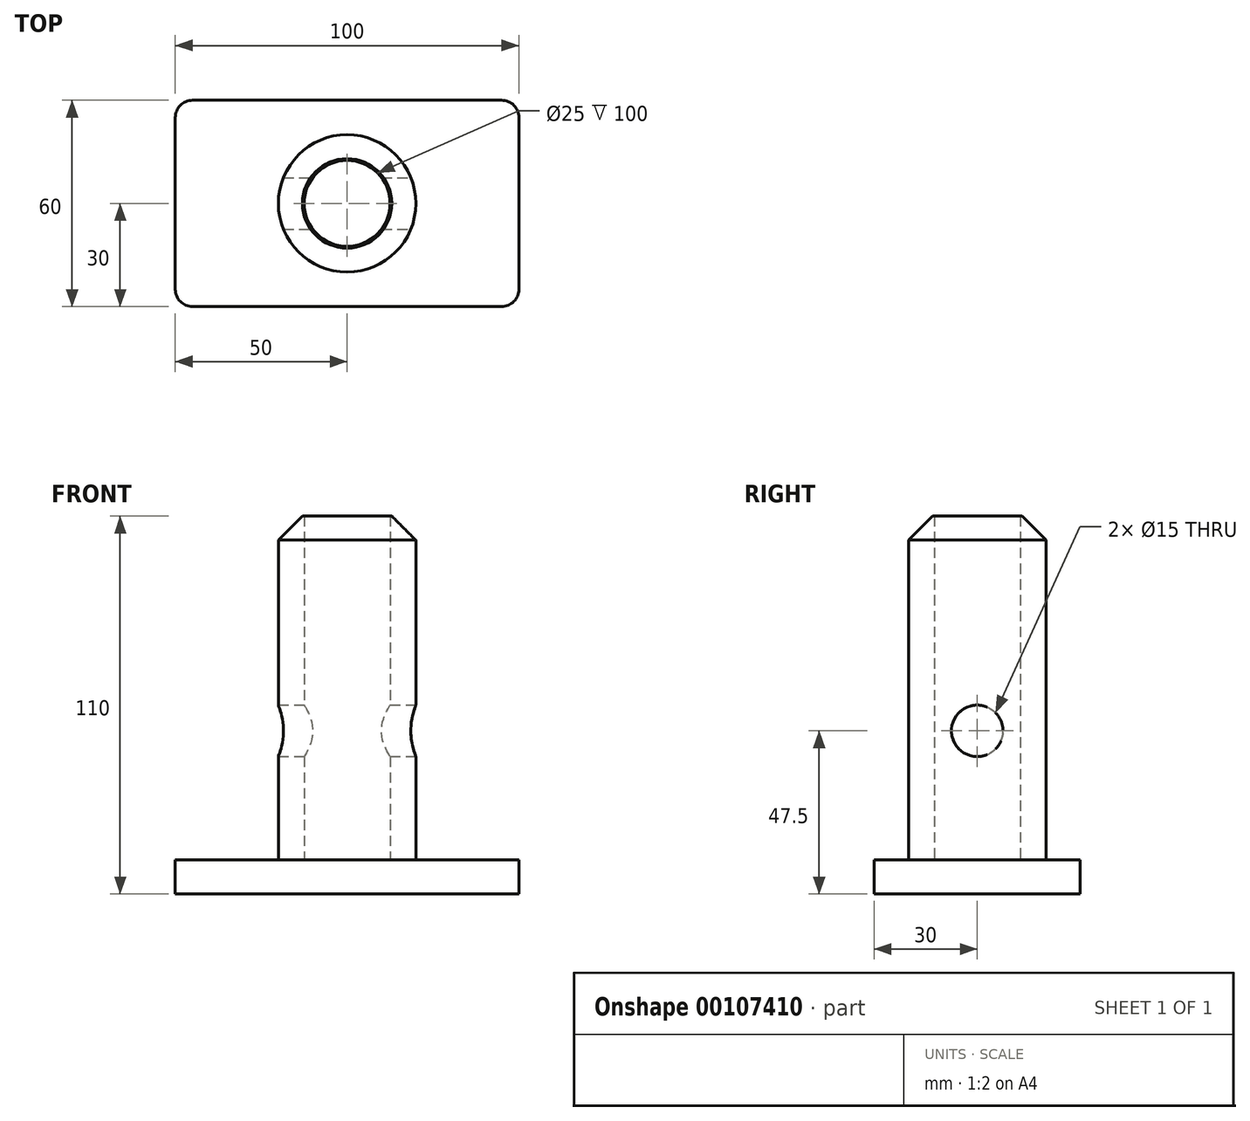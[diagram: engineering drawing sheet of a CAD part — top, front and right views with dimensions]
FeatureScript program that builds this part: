
annotation { "Feature Type Name" : "Feature", "Feature Type Description" : "" }
export const myFeature = defineFeature(function(context is Context, id is Id, definition is map)
    precondition{}
    {
        {
            var Q0;
            Q0=qCreatedBy(makeId("Top.planeOp"),FACE);
            var sketch = newSketch(context, id + "F0", { "sketchPlane" : qUnion([Q0])});
            skCircle(sketch, "E0", {"center": v(0, 0) * mm, "radius": 20 * mm});
            skCircle(sketch, "E1", {"center": v(0, 0) * mm, "radius": 12.5 * mm});
            skSolve(sketch);
        }
        {
            var Q0;
            Q0 = qSketchRegion(id + "F0", true);
            extrude(context, id + "F1", {"entities" : qUnion([Q0]), "depth" : 100 * mm});
        }
        {
            var Q0;
            Q0=qCreatedBy(makeId("Top.planeOp"),FACE);
            var sketch = newSketch(context, id + "F2", { "sketchPlane" : qUnion([Q0])});
            skLineSegment(sketch, "E2.bottom", {"start": v(50, -30) * mm, "end": v(-50, -30) * mm});
            skLineSegment(sketch, "E2.top", {"start": v(50, 30) * mm, "end": v(-50, 30) * mm});
            skLineSegment(sketch, "E2.left", {"start": v(50, -30) * mm, "end": v(50, 30) * mm});
            skLineSegment(sketch, "E2.right", {"start": v(-50, -30) * mm, "end": v(-50, 30) * mm});
            skPoint(sketch, "E2.middle", {"position": v(0, 0) * mm});
            skSolve(sketch);
        }
        {
            var Q0;
            Q0 = qSketchRegion(id + "F2", true);
            extrude(context, id + "F3", {"entities" : qUnion([Q0]), "operationType" : NewBodyOperationType.ADD, "oppositeDirection" : true, "depth" : 10 * mm});
        }
        {
            var Q0;
            Q0=makeQuery(id+"F3.opExtrude","SWEPT_EDGE",EDGE,{"disambiguationData":[OSD([sQuery(id+"F2.wireOp",EDGE,"E2.bottom"),sQuery(id+"F2.wireOp",EDGE,"E2.right")])]});
            var Q1;
            Q1=makeQuery(id+"F3.opExtrude","SWEPT_EDGE",EDGE,{"disambiguationData":[OSD([sQuery(id+"F2.wireOp",EDGE,"E2.bottom"),sQuery(id+"F2.wireOp",EDGE,"E2.left")])]});
            var Q2;
            Q2=makeQuery(id+"F3.opExtrude","SWEPT_EDGE",EDGE,{"disambiguationData":[OSD([sQuery(id+"F2.wireOp",EDGE,"E2.top"),sQuery(id+"F2.wireOp",EDGE,"E2.left")])]});
            var Q3;
            Q3=makeQuery(id+"F3.opExtrude","SWEPT_EDGE",EDGE,{"disambiguationData":[OSD([sQuery(id+"F2.wireOp",EDGE,"E2.top"),sQuery(id+"F2.wireOp",EDGE,"E2.right")])]});
            fillet(context, id + "F4", {"entities" : qUnion([Q0, Q1, Q2, Q3]), "radius" : 5 * mm, "tangentPropagation" : true, "allowEdgeOverflow" : false});
        }
        {
            var Q0;
            Q0=makeQuery(id+"F1.opExtrude","CAP_EDGE",EDGE,{"disambiguationData":[OSD([sQuery(id+"F0.wireOp",EDGE,"E0")])],"isStart":false});
            chamfer(context, id + "F5", {"entities" : qUnion([Q0]), "width" : 7 * mm, "tangentPropagation" : true});
        }
        {
            var Q0;
            Q0=qCreatedBy(makeId("Right.planeOp"),FACE);
            var sketch = newSketch(context, id + "F6", { "sketchPlane" : qUnion([Q0])});
            skCircle(sketch, "E3", {"center": v(0, 37.5) * mm, "radius": 7.5 * mm});
            skSolve(sketch);
        }
        {
            var Q0;
            Q0 = qSketchRegion(id + "F6", true);
            extrude(context, id + "F7", {"entities" : qUnion([Q0]), "operationType" : NewBodyOperationType.REMOVE, "endBound" : BoundingType.SYMMETRIC, "oppositeDirection" : true, "depth" : 40 * mm});
        }
    });
